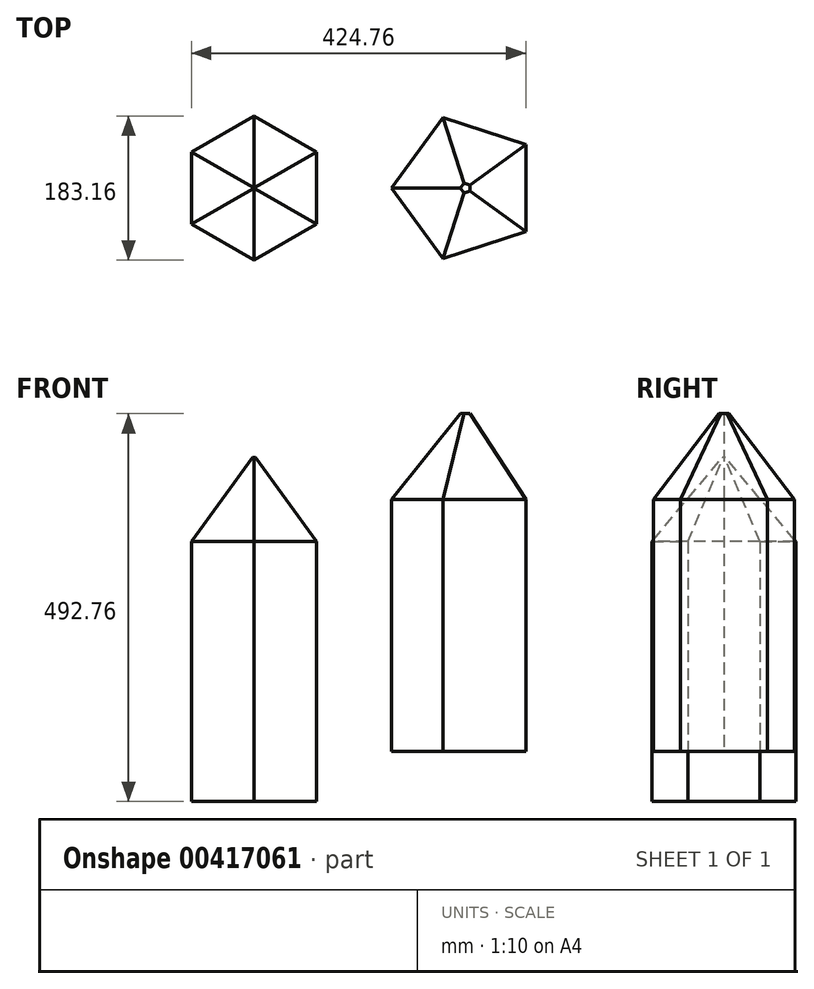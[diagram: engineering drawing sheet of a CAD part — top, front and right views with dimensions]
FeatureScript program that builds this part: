
annotation { "Feature Type Name" : "Feature", "Feature Type Description" : "" }
export const myFeature = defineFeature(function(context is Context, id is Id, definition is map)
    precondition{}
    {
        {
            var Q0;
            Q0=qCreatedBy(makeId("Top.planeOp"),FACE);
            var sketch = newSketch(context, id + "F0", { "sketchPlane" : qUnion([Q0])});
            skCircle(sketch, "E0.cCircle", {"center": v(0, 0) * mm, "radius": 76.34 * mm, "construction": true});
            skLineSegment(sketch, "E0.0", {"start": v(76.34, 55.46) * mm, "end": v(76.34, -55.46) * mm});
            skLineSegment(sketch, "E0.1", {"start": v(76.34, -55.46) * mm, "end": v(-29.16, -89.74) * mm});
            skLineSegment(sketch, "E0.2", {"start": v(-29.16, -89.74) * mm, "end": v(-94.36, 0) * mm});
            skLineSegment(sketch, "E0.3", {"start": v(-94.36, 0) * mm, "end": v(-29.16, 89.74) * mm});
            skLineSegment(sketch, "E0.4", {"start": v(-29.16, 89.74) * mm, "end": v(76.34, 55.46) * mm});
            skPoint(sketch, "E0.0.midPoint", {"position": v(76.34, 0) * mm});
            skSolve(sketch);
        }
        {
            var Q0;
            Q0 = qSketchRegion(id + "F0", true);
            extrude(context, id + "F1", {"entities" : qUnion([Q0]), "depth" : 190.5 * mm});
        }
        {
            var Q0;
            Q0=makeQuery(id+"F1.opExtrude","CAP_EDGE",EDGE,{"disambiguationData":[OSD([sQuery(id+"F0.wireOp",EDGE,"E0.2")])],"isStart":false});
            var Q1;
            Q1=makeQuery(id+"F1.opExtrude","CAP_EDGE",EDGE,{"disambiguationData":[OSD([sQuery(id+"F0.wireOp",EDGE,"E0.1")])],"isStart":false});
            var Q2;
            Q2=makeQuery(id+"F1.opExtrude","CAP_EDGE",EDGE,{"disambiguationData":[OSD([sQuery(id+"F0.wireOp",EDGE,"E0.0")])],"isStart":false});
            var Q3;
            Q3=makeQuery(id+"F1.opExtrude","CAP_EDGE",EDGE,{"disambiguationData":[OSD([sQuery(id+"F0.wireOp",EDGE,"E0.4")])],"isStart":false});
            var Q4;
            Q4=makeQuery(id+"F1.opExtrude","CAP_EDGE",EDGE,{"disambiguationData":[OSD([sQuery(id+"F0.wireOp",EDGE,"E0.3")])],"isStart":false});
            chamfer(context, id + "F2", {"entities" : qUnion([Q0, Q1, Q2, Q3, Q4]), "chamferType" : ChamferType.OFFSET_ANGLE, "width" : 109.22 * mm, "oppositeDirection" : false, "angle" : 33 * degree});
        }
        {
            var Q0;
            Q0=makeQuery(id+"F1.opExtrude","CAP_FACE",FACE,{"disambiguationData":[OSD([sQuery(id+"F0.wireOp",EDGE,"E0.0"),sQuery(id+"F0.wireOp",EDGE,"E0.1"),sQuery(id+"F0.wireOp",EDGE,"E0.2"),sQuery(id+"F0.wireOp",EDGE,"E0.3"),sQuery(id+"F0.wireOp",EDGE,"E0.4")])],"isStart":true});
            extrude(context, id + "F3", {"entities" : qUnion([Q0]), "operationType" : NewBodyOperationType.ADD, "depth" : 238.76 * mm});
        }
        {
            var Q0;
            Q0=qCreatedBy(makeId("Top.planeOp"),FACE);
            var sketch = newSketch(context, id + "F4", { "sketchPlane" : qUnion([Q0])});
            skCircle(sketch, "E1.cCircle", {"center": v(-269.1, 0) * mm, "radius": 79.31 * mm, "construction": true});
            skLineSegment(sketch, "E1.0", {"start": v(-189.8, 45.8) * mm, "end": v(-189.8, -45.8) * mm});
            skLineSegment(sketch, "E1.1", {"start": v(-189.8, -45.8) * mm, "end": v(-269.1, -91.58) * mm});
            skLineSegment(sketch, "E1.2", {"start": v(-269.1, -91.58) * mm, "end": v(-348.42, -45.8) * mm});
            skLineSegment(sketch, "E1.3", {"start": v(-348.42, -45.8) * mm, "end": v(-348.42, 45.8) * mm});
            skLineSegment(sketch, "E1.4", {"start": v(-348.42, 45.8) * mm, "end": v(-269.1, 91.58) * mm});
            skLineSegment(sketch, "E1.5", {"start": v(-269.1, 91.58) * mm, "end": v(-189.8, 45.8) * mm});
            skPoint(sketch, "E1.0.midPoint", {"position": v(-189.8, 0) * mm});
            skSolve(sketch);
        }
        {
            var Q0;
            Q0 = qSketchRegion(id + "F4", true);
            extrude(context, id + "F5", {"entities" : qUnion([Q0]), "depth" : 134.62 * mm});
        }
        {
            var Q0;
            Q0=makeQuery(id+"F5.opExtrude","CAP_EDGE",EDGE,{"disambiguationData":[OSD([sQuery(id+"F4.wireOp",EDGE,"E1.2")])],"isStart":false});
            var Q1;
            Q1=makeQuery(id+"F5.opExtrude","CAP_EDGE",EDGE,{"disambiguationData":[OSD([sQuery(id+"F4.wireOp",EDGE,"E1.1")])],"isStart":false});
            var Q2;
            Q2=makeQuery(id+"F5.opExtrude","CAP_EDGE",EDGE,{"disambiguationData":[OSD([sQuery(id+"F4.wireOp",EDGE,"E1.0")])],"isStart":false});
            var Q3;
            Q3=makeQuery(id+"F5.opExtrude","CAP_EDGE",EDGE,{"disambiguationData":[OSD([sQuery(id+"F4.wireOp",EDGE,"E1.5")])],"isStart":false});
            var Q4;
            Q4=makeQuery(id+"F5.opExtrude","CAP_EDGE",EDGE,{"disambiguationData":[OSD([sQuery(id+"F4.wireOp",EDGE,"E1.4")])],"isStart":false});
            var Q5;
            Q5=makeQuery(id+"F5.opExtrude","CAP_EDGE",EDGE,{"disambiguationData":[OSD([sQuery(id+"F4.wireOp",EDGE,"E1.3")])],"isStart":false});
            chamfer(context, id + "F6", {"entities" : qUnion([Q0, Q1, Q2, Q3, Q4, Q5]), "chamferType" : ChamferType.OFFSET_ANGLE, "width" : 106.68 * mm, "oppositeDirection" : false, "angle" : 36 * degree, "tangentPropagation" : true});
        }
        {
            var Q0;
            Q0=makeQuery(id+"F5.opExtrude","CAP_FACE",FACE,{"disambiguationData":[OSD([sQuery(id+"F4.wireOp",EDGE,"E1.0"),sQuery(id+"F4.wireOp",EDGE,"E1.1"),sQuery(id+"F4.wireOp",EDGE,"E1.2"),sQuery(id+"F4.wireOp",EDGE,"E1.3"),sQuery(id+"F4.wireOp",EDGE,"E1.4"),sQuery(id+"F4.wireOp",EDGE,"E1.5")])],"isStart":true});
            extrude(context, id + "F7", {"entities" : qUnion([Q0]), "operationType" : NewBodyOperationType.ADD, "depth" : 302.26 * mm});
        }
    });
